# Revit family: 63_UN_LF_Surface-Mounted-Titan-Angle-30-7_LI
name_source: partatom
category: Lighting Fixtures
units: mm (PartAtom-declared; Revit-internal decimal feet)

## family parameters
Always vertical = Yes
Cut with Voids When Loaded = Yes
Light Source = No
OmniClass Number = 23.80.70.11.14.11
OmniClass Title = Downlights
Part Type = Normal
Room Calculation Point = Yes
Round Connector Dimension = Use Diameter
Shared = No
Work Plane-Based = No

## types (2) — shared parameters
Assembly Code = 63.0
Housing_Material = Plastic, Opaque Black
IfcExportAs = IfcLightFixtureType
IfcExportType = USERDEFINED
Lamp = LED
Manufacturer = Light International
Model = TITAN Angle 30
URL = https://lightinternational.nl
Voltage = 230 V

## per-type parameters (varying)
| type | Apparent Load | Light Source | Luminous Flux (lm) | Type Comments | Wattage Comments |
| TA3071 - Wall mounted | 6 VA | TA307 Geometry : TA3071 Geometry | 1062 lm | TA3071 | 6.2W |
| TA3072 - Wall mounted | 12 VA | TA307 Geometry : TA3072 Geometry | 2133 lm | TA3072 | 11.8W |

## geometry (parser evidence)
native form markers: Sweep x19
no freeform markers — native parametric forms only
